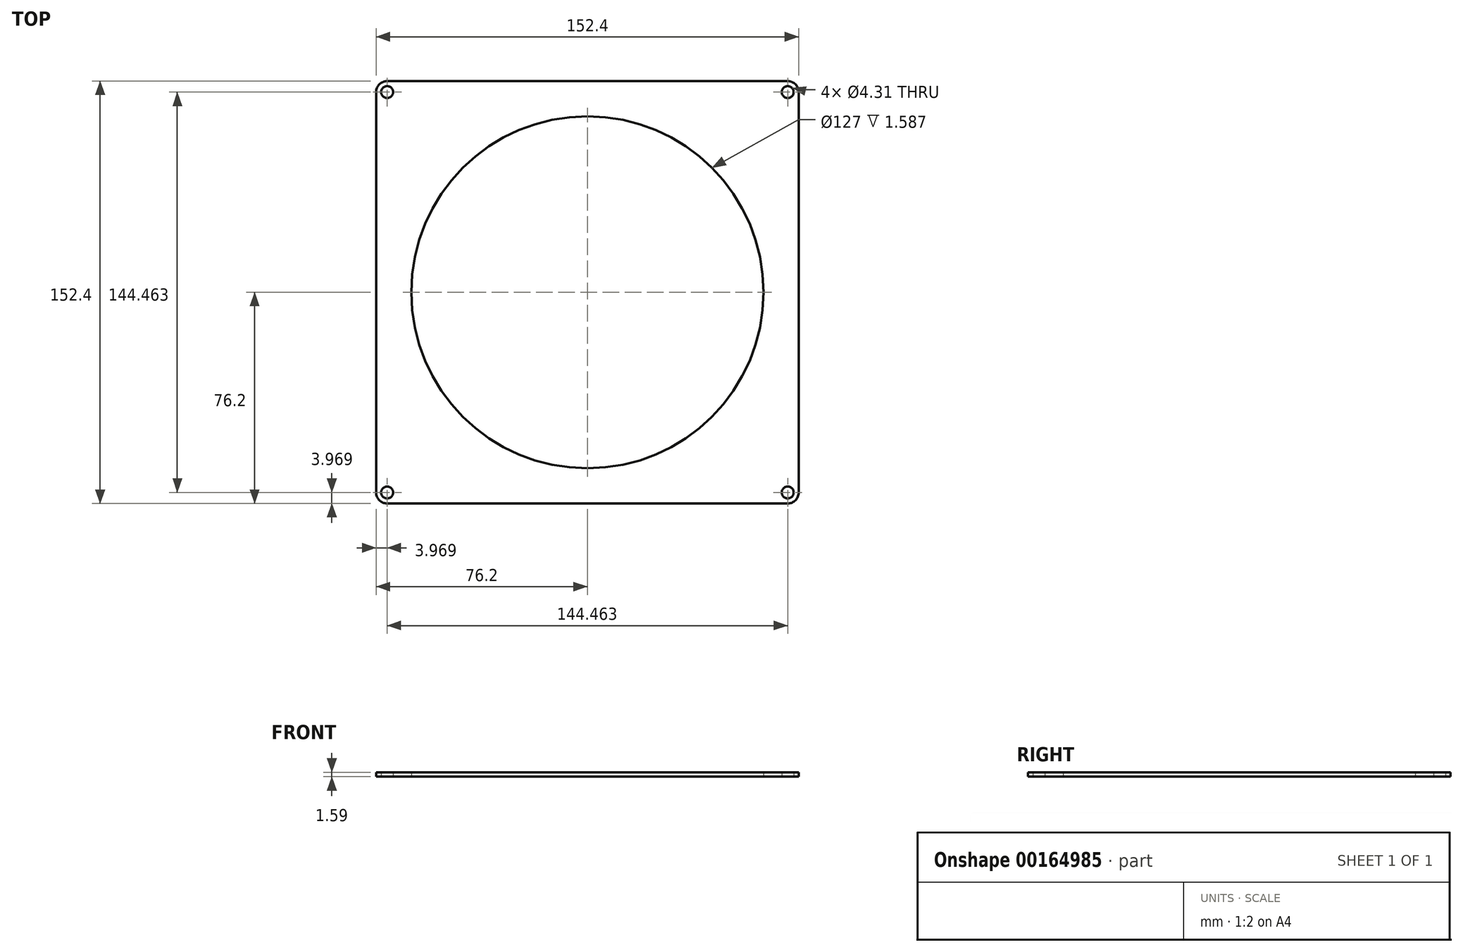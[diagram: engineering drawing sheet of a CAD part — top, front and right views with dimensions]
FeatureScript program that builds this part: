
annotation { "Feature Type Name" : "Feature", "Feature Type Description" : "" }
export const myFeature = defineFeature(function(context is Context, id is Id, definition is map)
    precondition{}
    {
        {
            var Q0;
            Q0=qCreatedBy(makeId("Top.planeOp"),FACE);
            var sketch = newSketch(context, id + "F0", { "sketchPlane" : qUnion([Q0])});
            skCircle(sketch, "E0", {"center": v(0, 0) * mm, "radius": 63.5 * mm});
            skLineSegment(sketch, "E1.bottom", {"start": v(76.2, 76.2) * mm, "end": v(-76.2, 76.2) * mm});
            skLineSegment(sketch, "E1.top", {"start": v(76.2, -76.2) * mm, "end": v(-76.2, -76.2) * mm});
            skLineSegment(sketch, "E1.left", {"start": v(76.2, 76.2) * mm, "end": v(76.2, -76.2) * mm});
            skLineSegment(sketch, "E1.right", {"start": v(-76.2, 76.2) * mm, "end": v(-76.2, -76.2) * mm});
            skLineSegment(sketch, "E2.bottom", {"start": v(72.23, 72.23) * mm, "end": v(-72.23, 72.23) * mm, "construction": true});
            skLineSegment(sketch, "E2.top", {"start": v(72.23, -72.23) * mm, "end": v(-72.23, -72.23) * mm, "construction": true});
            skLineSegment(sketch, "E2.left", {"start": v(72.23, 72.23) * mm, "end": v(72.23, -72.23) * mm, "construction": true});
            skLineSegment(sketch, "E2.right", {"start": v(-72.23, 72.23) * mm, "end": v(-72.23, -72.23) * mm, "construction": true});
            skCircle(sketch, "E3", {"center": v(-72.23, 72.23) * mm, "radius": 2.15 * mm});
            skCircle(sketch, "E4", {"center": v(72.23, 72.23) * mm, "radius": 2.15 * mm});
            skCircle(sketch, "E5", {"center": v(72.23, -72.23) * mm, "radius": 2.15 * mm});
            skCircle(sketch, "E6", {"center": v(-72.23, -72.23) * mm, "radius": 2.15 * mm});
            skSolve(sketch);
        }
        {
            var Q0;
            Q0 = qSketchRegion(id + "F0", true);
            extrude(context, id + "F1", {"entities" : qUnion([Q0]), "depth" : 1.59 * mm});
        }
        {
            var Q0;
            Q0=makeQuery(id+"F1.opExtrude","SWEPT_EDGE",EDGE,{"disambiguationData":[OSD([sQuery(id+"F0.wireOp",EDGE,"E1.bottom"),sQuery(id+"F0.wireOp",EDGE,"E1.right")])]});
            var Q1;
            Q1=makeQuery(id+"F1.opExtrude","SWEPT_EDGE",EDGE,{"disambiguationData":[OSD([sQuery(id+"F0.wireOp",EDGE,"E1.bottom"),sQuery(id+"F0.wireOp",EDGE,"E1.left")])]});
            var Q2;
            Q2=makeQuery(id+"F1.opExtrude","SWEPT_EDGE",EDGE,{"disambiguationData":[OSD([sQuery(id+"F0.wireOp",EDGE,"E1.top"),sQuery(id+"F0.wireOp",EDGE,"E1.left")])]});
            var Q3;
            Q3=makeQuery(id+"F1.opExtrude","SWEPT_EDGE",EDGE,{"disambiguationData":[OSD([sQuery(id+"F0.wireOp",EDGE,"E1.top"),sQuery(id+"F0.wireOp",EDGE,"E1.right")])]});
            fillet(context, id + "F2", {"entities" : qUnion([Q0, Q1, Q2, Q3]), "radius" : 3.97 * mm, "tangentPropagation" : true, "allowEdgeOverflow" : false});
        }
    });
